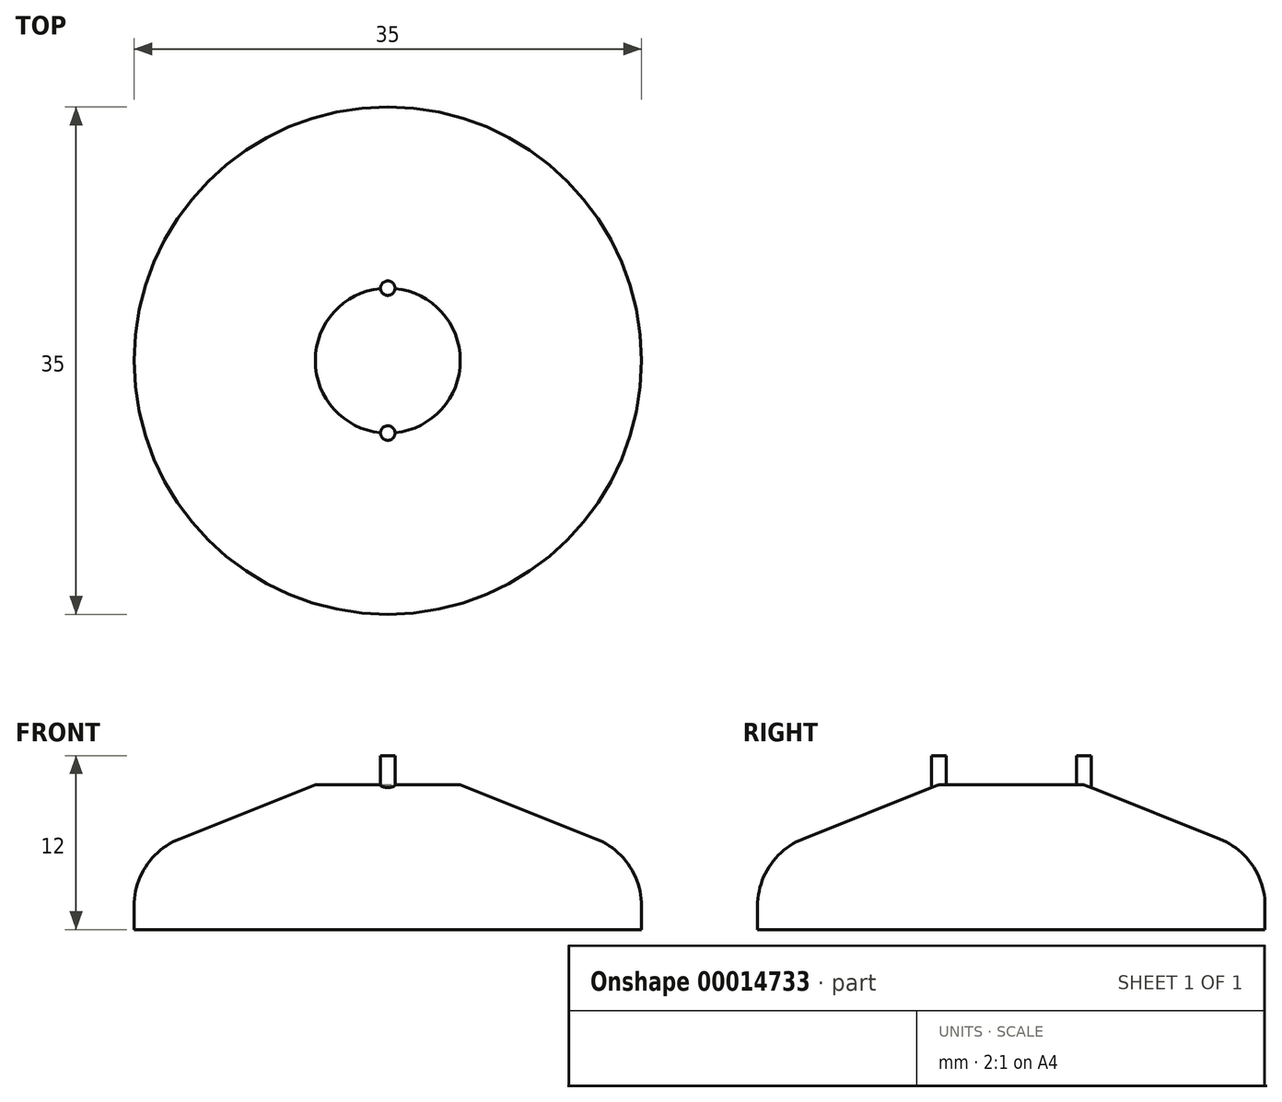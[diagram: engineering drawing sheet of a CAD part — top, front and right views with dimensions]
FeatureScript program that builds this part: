
annotation { "Feature Type Name" : "Feature", "Feature Type Description" : "" }
export const myFeature = defineFeature(function(context is Context, id is Id, definition is map)
    precondition{}
    {
        {
            var Q0;
            Q0=qCreatedBy(makeId("Front.planeOp"),FACE);
            var sketch = newSketch(context, id + "F0", { "sketchPlane" : qUnion([Q0])});
            skLineSegment(sketch, "E0", {"start": v(0, 0) * mm, "end": v(-17.5, 0) * mm});
            skLineSegment(sketch, "E1", {"start": v(-17.5, 0) * mm, "end": v(-17.5, 5) * mm});
            skLineSegment(sketch, "E2", {"start": v(-17.5, 5) * mm, "end": v(-5, 10) * mm});
            skLineSegment(sketch, "E3", {"start": v(-5, 10) * mm, "end": v(0, 10) * mm});
            skLineSegment(sketch, "E4", {"start": v(0, 10) * mm, "end": v(0, 0) * mm});
            skSolve(sketch);
        }
        {
            var Q0;
            Q0=qSketchRegion(id+"F0",true);
            var Q1;
            Q1=sQuery(id+"F0.wireOp",EDGE,"E4");
            revolve(context, id + "F1", {"entities" : qUnion([Q0]), "axis" : qUnion([Q1]), "revolveType" : RevolveType.FULL});
        }
        {
            var Q0;
            Q0=makeQuery(id+"F1.opRevolve","SWEPT_FACE",FACE,{"disambiguationData":[OSD([sQuery(id+"F0.wireOp",EDGE,"E3")])]});
            var sketch = newSketch(context, id + "F2", { "sketchPlane" : qUnion([Q0])});
            skCircle(sketch, "E5", {"center": v(0, 5) * mm, "radius": 0.5 * mm});
            skCircle(sketch, "E6", {"center": v(0, -5) * mm, "radius": 0.5 * mm});
            skSolve(sketch);
        }
        {
            var Q0;
            Q0=qSketchRegion(id+"F2",true);
            extrude(context, id + "F3", {"entities" : qUnion([Q0]), "operationType" : NewBodyOperationType.ADD, "depth" : 2 * mm, "hasSecondDirection" : true, "secondDirectionOppositeDirection" : true, "secondDirectionDepth" : 2 * mm});
        }
        {
            var Q0;
            Q0=makeQuery(id+"F1.opRevolve","SWEPT_EDGE",EDGE,{"disambiguationData":[OSD([sQuery(id+"F0.wireOp",EDGE,"E1"),sQuery(id+"F0.wireOp",EDGE,"E2")])]});
            fillet(context, id + "F4", {"entities" : qUnion([Q0]), "radius" : 5 * mm, "tangentPropagation" : true, "allowEdgeOverflow" : false});
        }
    });
